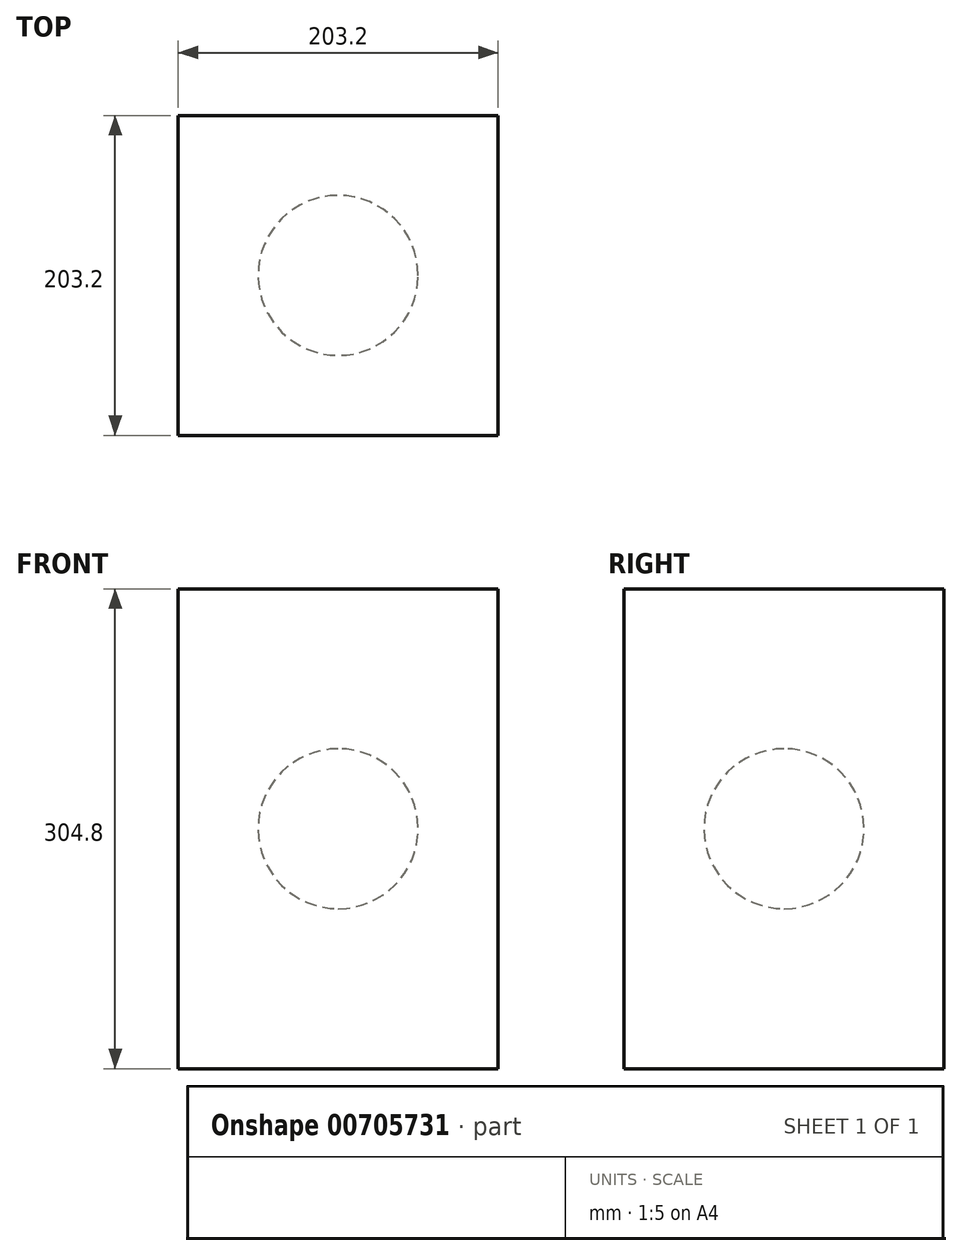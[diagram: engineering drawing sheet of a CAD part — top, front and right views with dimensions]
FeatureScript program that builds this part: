
annotation { "Feature Type Name" : "Feature", "Feature Type Description" : "" }
export const myFeature = defineFeature(function(context is Context, id is Id, definition is map)
    precondition{}
    {
        {
            var Q0;
            Q0=qCreatedBy(makeId("Front.planeOp"),FACE);
            var sketch = newSketch(context, id + "F0", { "sketchPlane" : qUnion([Q0])});
            skLineSegment(sketch, "E0.bottom", {"start": v(101.6, 152.4) * mm, "end": v(-101.6, 152.4) * mm});
            skLineSegment(sketch, "E0.top", {"start": v(101.6, -152.4) * mm, "end": v(-101.6, -152.4) * mm});
            skLineSegment(sketch, "E0.left", {"start": v(101.6, 152.4) * mm, "end": v(101.6, -152.4) * mm});
            skLineSegment(sketch, "E0.right", {"start": v(-101.6, 152.4) * mm, "end": v(-101.6, -152.4) * mm});
            skPoint(sketch, "E0.middle", {"position": v(0, 0) * mm});
            skSolve(sketch);
        }
        {
            var Q0;
            Q0 = qSketchRegion(id + "F0", true);
            extrude(context, id + "F1", {"entities" : qUnion([Q0]), "endBound" : BoundingType.SYMMETRIC, "oppositeDirection" : true, "depth" : 203.2 * mm, "offsetDistance" : 25.4 * mm});
        }
        {
            var Q0;
            Q0=qCreatedBy(makeId("Front.planeOp"),FACE);
            var sketch = newSketch(context, id + "F2", { "sketchPlane" : qUnion([Q0])});
            skCircle(sketch, "E1", {"center": v(0, 0) * mm, "radius": 50.8 * mm});
            skLineSegment(sketch, "E2", {"start": v(0, 50.8) * mm, "end": v(0, -50.8) * mm});
            skSolve(sketch);
        }
        {
            var Q0;
            {var subQ0=sQuery(id+"F2.wireOp",EDGE,"E2");Q0=makeQuery(id+"F2.imprint","IMPRINT",FACE,{"disambiguationData":[TD([[makeQuery(id+"F2.imprint","IMPRINT",EDGE,{"derivedFrom":subQ0}),-1.0]])]});}
            var Q1;
            Q1=sQuery(id+"F2.wireOp",EDGE,"E2");
            revolve(context, id + "F3", {"surfaceOperationType" : NewSurfaceOperationType.NEW, "entities" : qUnion([Q0]), "axis" : qUnion([Q1]), "revolveType" : RevolveType.FULL});
        }
    });
